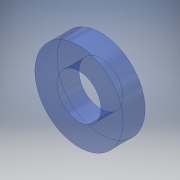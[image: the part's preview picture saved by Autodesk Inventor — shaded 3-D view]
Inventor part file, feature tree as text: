
AUTODESK INVENTOR PART (.ipt)
format: ipt  version: 2019.4 (Build 234330000, 330)  size: 104,448 bytes
history: native  units: mm
features: extrude x1, sketch x1
ambient origin geometry x8: Origin, YZ Plane, XZ Plane, XY Plane, X Axis, Y Axis, Z Axis, Center Point
bodies: Solid1 (feature_tree)
feature tree (2):
  extrude  "Extrusion1"  Depth=3.0mm
  sketch  "Sketch1"  dims[d0=6.0mm d1=12.0mm d2=3.0mm d3=0.0mm]
